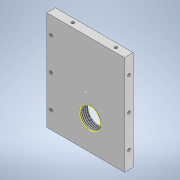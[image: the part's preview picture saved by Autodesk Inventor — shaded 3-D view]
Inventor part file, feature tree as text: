
AUTODESK INVENTOR PART (.ipt)
format: ipt  version: 2022.2 (Build 262287030, 287C)  size: 274,944 bytes
history: native  units: in
note: dims shown in document units (in); Inventor stores cm internally (conversion verified against a paired STEP export)
features: sketch x8, hole x5, extrude x1, plane x1, helix x1
ambient origin geometry x8: Origin, YZ Plane, XZ Plane, XY Plane, X Axis, Y Axis, Z Axis, Center Point
bodies: Solid1 (feature_tree)
feature tree (16):
  extrude  "Extrusion1"  Depth=4.5276in
  hole  "Hole1"  [1 undecoded]
  hole  "Hole2"  [1 undecoded]
  hole  "Hole3"  [1 undecoded]
  hole  "Hole4"  [1 undecoded]
  hole  "Hole5"  [1 undecoded]
  sketch  "Sketch9"  dims[d38=0.7874in d40=1.9685in d41=0.3937in d43=0.3937in]
  plane  "Work Plane1"
  helix  "Coil1"  [1 undecoded]
  sketch  "Sketch1"  dims[d0=3.5433in d1=4.5276in]
  sketch  "Sketch2"  dims[d2=0.3937in d3=0.0in d4=0.7874in]
  sketch  "Sketch3"  dims[d5=0.1969in d6=1.1811in d8=1.4764in d9=0.3937in d11=0.3937in]
  sketch  "Sketch4"  dims[d13=0.125in d14=0.2953in d15=0.1476in d16=0.0984in d17=90.0deg d18=0.1969in d19=0.0in d20=0.9843in]
  sketch  "Sketch5"  dims[d21=0.1969in d22=0.7874in d24=1.9685in d25=0.3937in d27=0.3937in]
  sketch  "Sketch8"  dims[d29=0.125in d30=0.2953in d31=0.1476in d32=0.0984in d33=90.0deg d34=0.1969in d35=0.0in d36=0.9843in d37=0.1969in]
  sketch  "Sketch10"  dims[d45=0.125in d46=0.2953in d47=0.1476in d48=0.0984in d49=90.0deg d50=0.1969in d51=0.0in d52=0.1969in d53=0.7874in d54=1.1811in d56=1.4764in d57=0.3937in d59=0.3937in d61=0.125in d62=0.2953in d63=0.1476in d64=0.0984in d65=90.0deg d66=0.1969in d67=0.0in d79=0.9449in d80=2.0819in d81=0.1476in d82=0.0984in d83=90.0deg d84=0.3937in d85=0.8108in d86=0.4724in d94=0.0787in d95=0.0394in d96=0.0in d97=0.3543in d98=0.0787in d99=0.3937in d100=2.3622in d101=0.0in d102=90.0deg d103=90.0deg d104=0.0in d105=0.0in d106=0.0079in]
note: 6 required parameter values undecoded (feature->parameter linkage not recoverable at this tier; creation-order binding heuristic only, values carry confidence <= 0.55)
